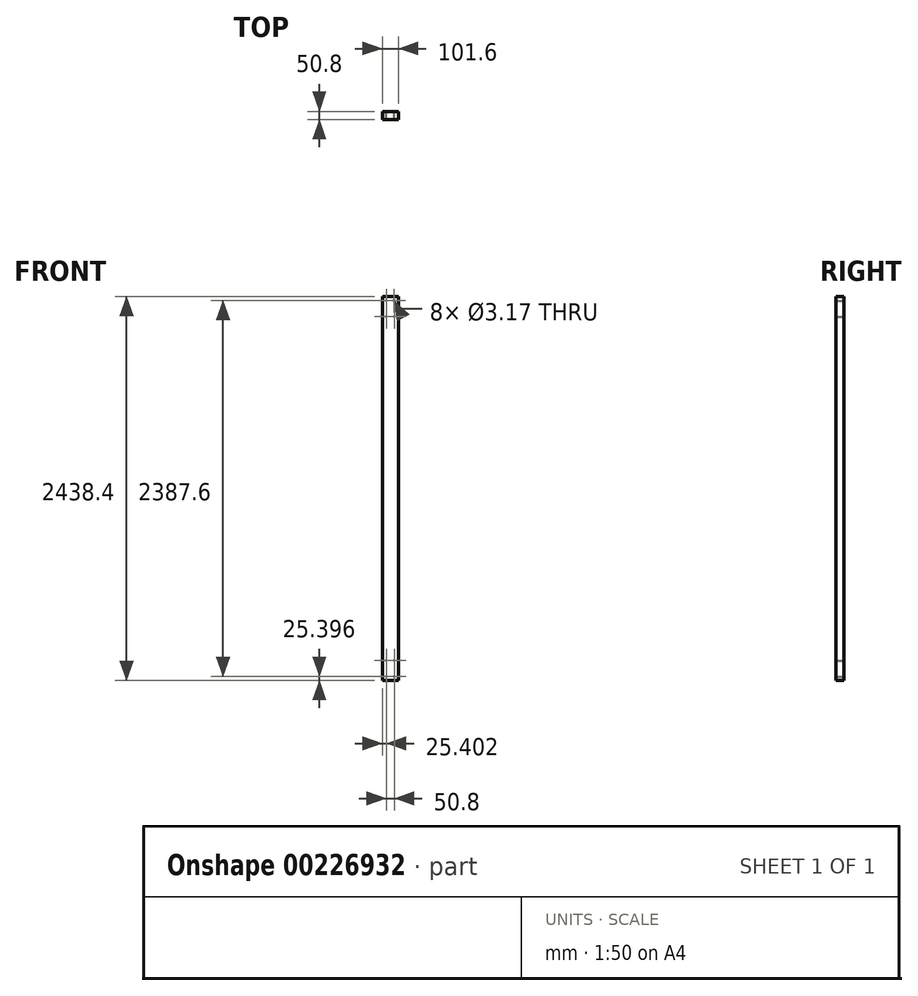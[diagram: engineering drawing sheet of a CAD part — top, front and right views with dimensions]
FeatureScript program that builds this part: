
annotation { "Feature Type Name" : "Feature", "Feature Type Description" : "" }
export const myFeature = defineFeature(function(context is Context, id is Id, definition is map)
    precondition{}
    {
        {
            var Q0;
            Q0=qCreatedBy(makeId("Front.planeOp"),FACE);
            var sketch = newSketch(context, id + "F0", { "sketchPlane" : qUnion([Q0])});
            skLineSegment(sketch, "E0.bottom", {"start": v(-336.83, -1146.2) * mm, "end": v(-235.23, -1146.2) * mm});
            skLineSegment(sketch, "E0.top", {"start": v(-336.83, 1292.2) * mm, "end": v(-235.23, 1292.2) * mm});
            skLineSegment(sketch, "E0.left", {"start": v(-336.83, -1146.2) * mm, "end": v(-336.83, 1292.2) * mm});
            skLineSegment(sketch, "E0.right", {"start": v(-235.23, -1146.2) * mm, "end": v(-235.23, 1292.2) * mm});
            skCircle(sketch, "E1", {"center": v(-311.43, 1266.8) * mm, "radius": 1.59 * mm});
            skCircle(sketch, "E2", {"center": v(-262.22, 1266.8) * mm, "radius": 1.59 * mm});
            skCircle(sketch, "E3", {"center": v(-260.63, 1165.2) * mm, "radius": 1.59 * mm});
            skCircle(sketch, "E4", {"center": v(-311.43, 1165.2) * mm, "radius": 1.59 * mm});
            skCircle(sketch, "E5", {"center": v(-260.63, -1120.8) * mm, "radius": 1.59 * mm});
            skCircle(sketch, "E6", {"center": v(-311.43, -1120.8) * mm, "radius": 1.59 * mm});
            skCircle(sketch, "E7", {"center": v(-311.43, -1019.2) * mm, "radius": 1.59 * mm});
            skCircle(sketch, "E8", {"center": v(-260.63, -1019.2) * mm, "radius": 1.59 * mm});
            skSolve(sketch);
        }
        {
            var Q0;
            Q0=makeQuery(id+"F0.imprint","IMPRINT",FACE,{"disambiguationData":[TD([[makeQuery(id+"F0.imprint","IMPRINT",EDGE,{"derivedFrom":sQuery(id+"F0.wireOp",EDGE,"E0.bottom")}),1.0]])]});
            extrude(context, id + "F1", {"entities" : qUnion([Q0]), "depth" : 50.8 * mm});
        }
    });
